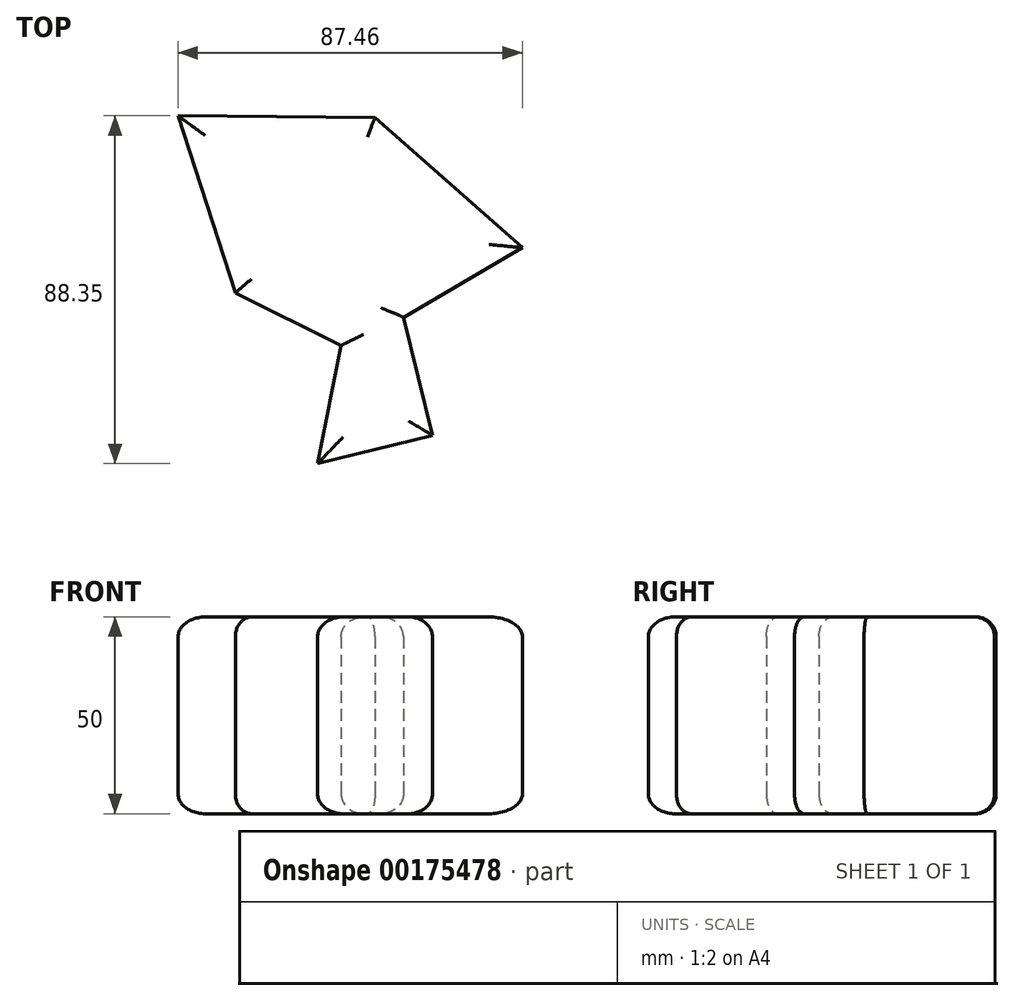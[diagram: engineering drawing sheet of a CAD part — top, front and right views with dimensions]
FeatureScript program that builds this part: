
annotation { "Feature Type Name" : "Feature", "Feature Type Description" : "" }
export const myFeature = defineFeature(function(context is Context, id is Id, definition is map)
    precondition{}
    {
        {
            var Q0;
            Q0=qCreatedBy(makeId("Top.planeOp"),FACE);
            var sketch = newSketch(context, id + "F0", { "sketchPlane" : qUnion([Q0])});
            skLineSegment(sketch, "E0", {"start": v(17.2, -33.48) * mm, "end": v(46.33, -26.34) * mm});
            skLineSegment(sketch, "E1", {"start": v(46.33, -26.34) * mm, "end": v(38.98, 3.66) * mm});
            skLineSegment(sketch, "E2", {"start": v(38.98, 3.66) * mm, "end": v(69.2, 21.34) * mm});
            skLineSegment(sketch, "E3", {"start": v(69.2, 21.34) * mm, "end": v(31.73, 54.45) * mm});
            skLineSegment(sketch, "E4", {"start": v(31.73, 54.45) * mm, "end": v(-18.27, 54.87) * mm});
            skLineSegment(sketch, "E5", {"start": v(-18.27, 54.87) * mm, "end": v(-3.72, 9.87) * mm});
            skLineSegment(sketch, "E6", {"start": v(-3.72, 9.87) * mm, "end": v(23.15, -3.48) * mm});
            skLineSegment(sketch, "E7", {"start": v(23.15, -3.48) * mm, "end": v(17.2, -33.48) * mm});
            skSolve(sketch);
        }
        {
            var Q0;
            Q0=makeQuery(id+"F0.imprint","IMPRINT",FACE,{"disambiguationData":[TD([[makeQuery(id+"F0.imprint","IMPRINT",EDGE,{"derivedFrom":sQuery(id+"F0.wireOp",EDGE,"E0")}),1.0]])]});
            extrude(context, id + "F1", {"entities" : qUnion([Q0]), "depth" : 50 * mm});
        }
        {
            var Q0;
            Q0=makeQuery(id+"F1.opExtrude","CAP_EDGE",EDGE,{"disambiguationData":[OSD([sQuery(id+"F0.wireOp",EDGE,"E3")])],"isStart":false});
            var Q1;
            Q1=makeQuery(id+"F1.opExtrude","CAP_EDGE",EDGE,{"disambiguationData":[OSD([sQuery(id+"F0.wireOp",EDGE,"E4")])],"isStart":false});
            var Q2;
            Q2=makeQuery(id+"F1.opExtrude","CAP_EDGE",EDGE,{"disambiguationData":[OSD([sQuery(id+"F0.wireOp",EDGE,"E2")])],"isStart":false});
            var Q3;
            Q3=makeQuery(id+"F1.opExtrude","CAP_EDGE",EDGE,{"disambiguationData":[OSD([sQuery(id+"F0.wireOp",EDGE,"E1")])],"isStart":false});
            var Q4;
            Q4=makeQuery(id+"F1.opExtrude","CAP_EDGE",EDGE,{"disambiguationData":[OSD([sQuery(id+"F0.wireOp",EDGE,"E0")])],"isStart":false});
            var Q5;
            Q5=makeQuery(id+"F1.opExtrude","CAP_EDGE",EDGE,{"disambiguationData":[OSD([sQuery(id+"F0.wireOp",EDGE,"E7")])],"isStart":false});
            var Q6;
            Q6=makeQuery(id+"F1.opExtrude","CAP_EDGE",EDGE,{"disambiguationData":[OSD([sQuery(id+"F0.wireOp",EDGE,"E6")])],"isStart":false});
            var Q7;
            Q7=makeQuery(id+"F1.opExtrude","CAP_EDGE",EDGE,{"disambiguationData":[OSD([sQuery(id+"F0.wireOp",EDGE,"E5")])],"isStart":false});
            var Q8;
            Q8=makeQuery(id+"F1.opExtrude","CAP_EDGE",EDGE,{"disambiguationData":[OSD([sQuery(id+"F0.wireOp",EDGE,"E3")])],"isStart":true});
            var Q9;
            Q9=makeQuery(id+"F1.opExtrude","CAP_EDGE",EDGE,{"disambiguationData":[OSD([sQuery(id+"F0.wireOp",EDGE,"E4")])],"isStart":true});
            var Q10;
            Q10=makeQuery(id+"F1.opExtrude","CAP_EDGE",EDGE,{"disambiguationData":[OSD([sQuery(id+"F0.wireOp",EDGE,"E1")])],"isStart":true});
            var Q11;
            Q11=makeQuery(id+"F1.opExtrude","CAP_EDGE",EDGE,{"disambiguationData":[OSD([sQuery(id+"F0.wireOp",EDGE,"E5")])],"isStart":true});
            var Q12;
            Q12=makeQuery(id+"F1.opExtrude","CAP_EDGE",EDGE,{"disambiguationData":[OSD([sQuery(id+"F0.wireOp",EDGE,"E6")])],"isStart":true});
            var Q13;
            Q13=makeQuery(id+"F1.opExtrude","CAP_EDGE",EDGE,{"disambiguationData":[OSD([sQuery(id+"F0.wireOp",EDGE,"E7")])],"isStart":true});
            var Q14;
            Q14=makeQuery(id+"F1.opExtrude","CAP_EDGE",EDGE,{"disambiguationData":[OSD([sQuery(id+"F0.wireOp",EDGE,"E0")])],"isStart":true});
            var Q15;
            Q15=makeQuery(id+"F1.opExtrude","CAP_EDGE",EDGE,{"disambiguationData":[OSD([sQuery(id+"F0.wireOp",EDGE,"E2")])],"isStart":true});
            fillet(context, id + "F2", {"entities" : qUnion([Q0, Q1, Q2, Q3, Q4, Q5, Q6, Q7, Q8, Q9, Q10, Q11, Q12, Q13, Q14, Q15]), "radius" : 5 * mm, "tangentPropagation" : true, "allowEdgeOverflow" : false});
        }
    });
